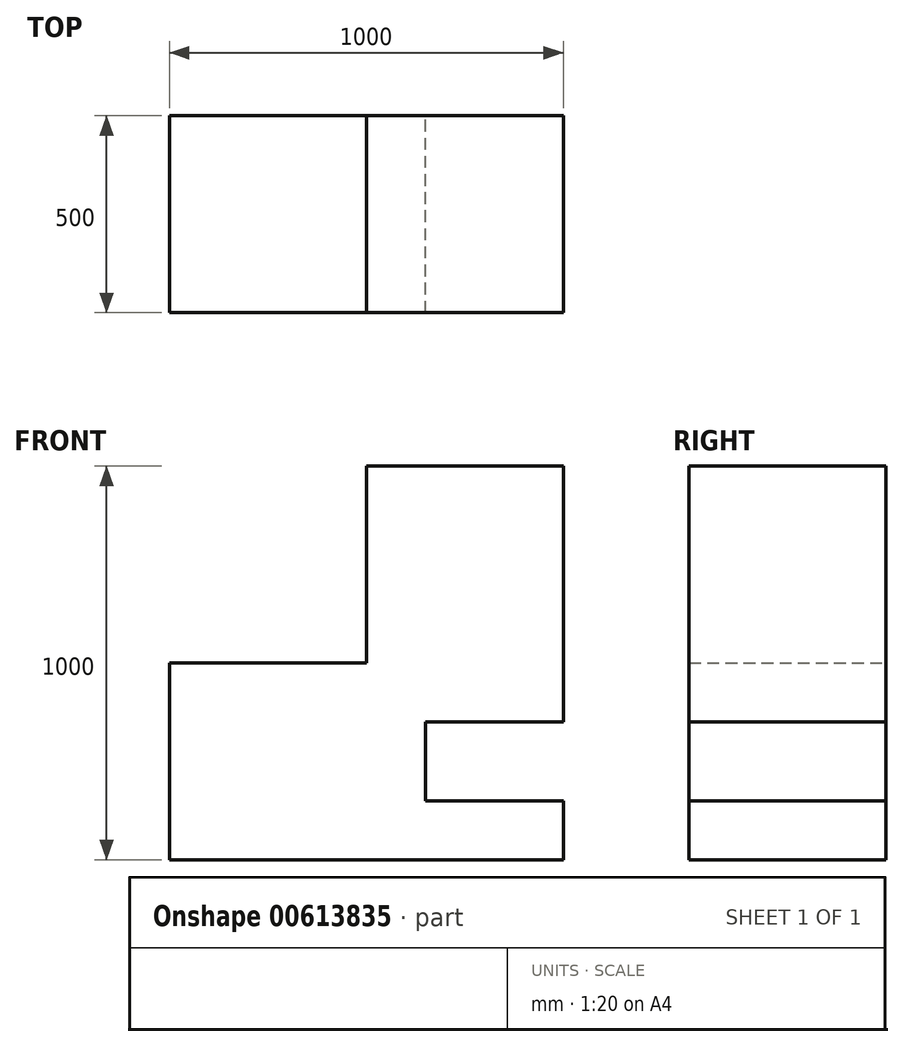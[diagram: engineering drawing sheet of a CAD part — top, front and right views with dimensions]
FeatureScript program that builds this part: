
annotation { "Feature Type Name" : "Feature", "Feature Type Description" : "" }
export const myFeature = defineFeature(function(context is Context, id is Id, definition is map)
    precondition{}
    {
        {
            var Q0;
            Q0=qCreatedBy(makeId("Front.planeOp"),FACE);
            var sketch = newSketch(context, id + "F0", { "sketchPlane" : qUnion([Q0])});
            skLineSegment(sketch, "E0", {"start": v(0, 0) * mm, "end": v(-1000, 0) * mm});
            skLineSegment(sketch, "E1", {"start": v(-1000, 0) * mm, "end": v(-1000, 500) * mm});
            skLineSegment(sketch, "E2", {"start": v(-1000, 500) * mm, "end": v(-500, 500) * mm});
            skLineSegment(sketch, "E3", {"start": v(-500, 500) * mm, "end": v(-500, 1000) * mm});
            skLineSegment(sketch, "E4", {"start": v(-500, 1000) * mm, "end": v(0, 1000) * mm});
            skLineSegment(sketch, "E5", {"start": v(0, 1000) * mm, "end": v(0, 350) * mm});
            skLineSegment(sketch, "E6", {"start": v(0, 350) * mm, "end": v(-350, 350) * mm});
            skLineSegment(sketch, "E7", {"start": v(-350, 350) * mm, "end": v(-350, 150) * mm});
            skLineSegment(sketch, "E8", {"start": v(-350, 150) * mm, "end": v(0, 150) * mm});
            skLineSegment(sketch, "E9", {"start": v(0, 150) * mm, "end": v(0, 0) * mm});
            skSolve(sketch);
        }
        {
            var Q0;
            Q0 = qSketchRegion(id + "F0", true);
            extrude(context, id + "F1", {"entities" : qUnion([Q0]), "depth" : 500 * mm, "offsetDistance" : 25 * mm});
        }
    });
